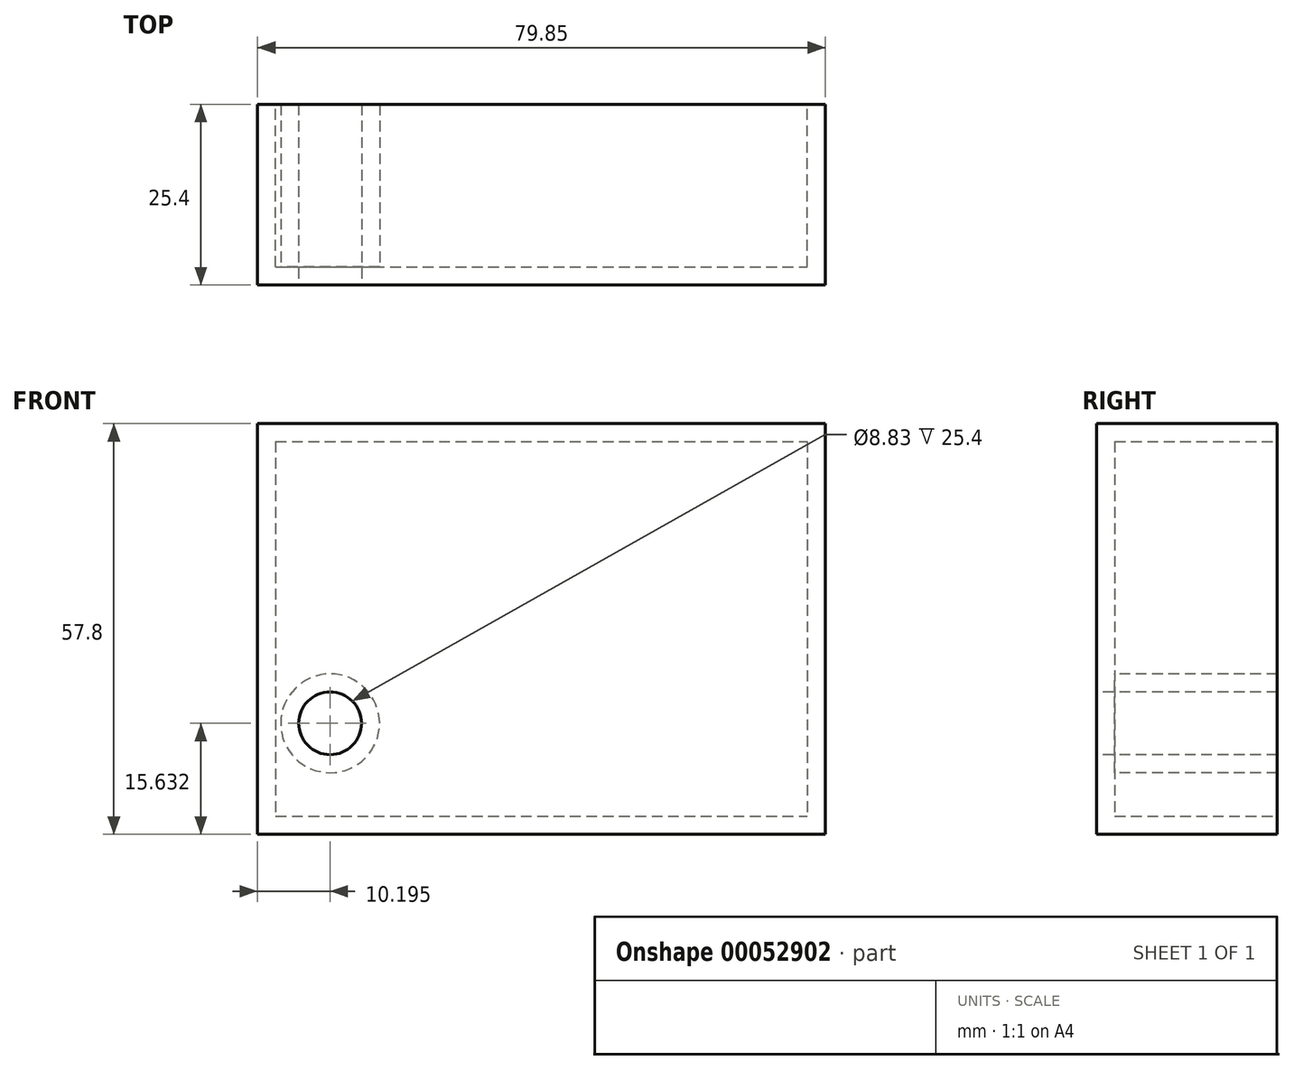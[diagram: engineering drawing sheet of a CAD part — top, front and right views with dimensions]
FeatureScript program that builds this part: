
annotation { "Feature Type Name" : "Feature", "Feature Type Description" : "" }
export const myFeature = defineFeature(function(context is Context, id is Id, definition is map)
    precondition{}
    {
        {
            var Q0;
            Q0=qCreatedBy(makeId("Front.planeOp"),FACE);
            var sketch = newSketch(context, id + "F0", { "sketchPlane" : qUnion([Q0])});
            skLineSegment(sketch, "E0.bottom", {"start": v(-90.04, 49.52) * mm, "end": v(-10.2, 49.52) * mm});
            skLineSegment(sketch, "E0.top", {"start": v(-90.04, -8.28) * mm, "end": v(-10.2, -8.28) * mm});
            skLineSegment(sketch, "E0.left", {"start": v(-90.04, 49.52) * mm, "end": v(-90.04, -8.28) * mm});
            skLineSegment(sketch, "E0.right", {"start": v(-10.2, 49.52) * mm, "end": v(-10.2, -8.28) * mm});
            skSolve(sketch);
        }
        {
            var Q0;
            Q0 = qSketchRegion(id + "F0", true);
            extrude(context, id + "F1", {"entities" : qUnion([Q0]), "depth" : 25.4 * mm});
        }
        {
            var Q0;
            Q0=makeQuery(id+"F1.opExtrude","CAP_FACE",FACE,{"disambiguationData":[OSD([sQuery(id+"F0.wireOp",EDGE,"E0.bottom"),sQuery(id+"F0.wireOp",EDGE,"E0.top"),sQuery(id+"F0.wireOp",EDGE,"E0.left"),sQuery(id+"F0.wireOp",EDGE,"E0.right")])],"isStart":false});
            var sketch = newSketch(context, id + "F2", { "sketchPlane" : qUnion([Q0])});
            skCircle(sketch, "E1", {"center": v(-79.85, 7.35) * mm, "radius": 4.41 * mm});
            skSolve(sketch);
        }
        {
            var Q0;
            Q0 = qSketchRegion(id + "F2", true);
            extrude(context, id + "F3", {"entities" : qUnion([Q0]), "operationType" : NewBodyOperationType.REMOVE, "oppositeDirection" : true, "depth" : 25.4 * mm});
        }
        {
            var Q0;
            Q0=makeQuery(id+"F1.opExtrude","CAP_FACE",FACE,{"disambiguationData":[OSD([sQuery(id+"F0.wireOp",EDGE,"E0.bottom"),sQuery(id+"F0.wireOp",EDGE,"E0.top"),sQuery(id+"F0.wireOp",EDGE,"E0.left"),sQuery(id+"F0.wireOp",EDGE,"E0.right")])],"isStart":true});
            shell(context, id + "F4", {"entities" : qUnion([Q0]), "thickness" : 2.54 * mm});
        }
    });
